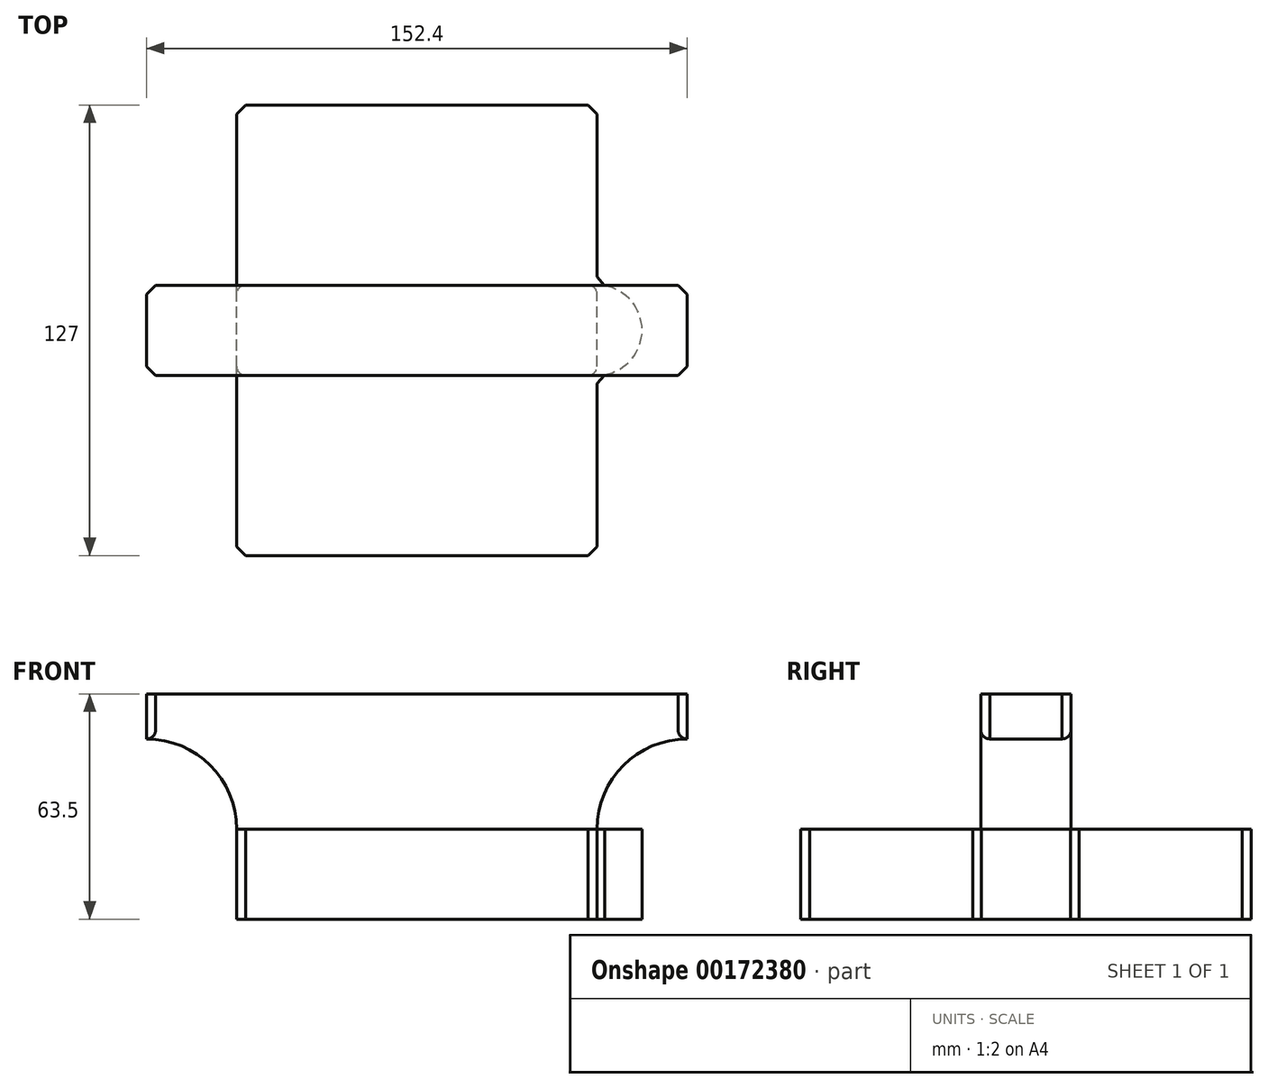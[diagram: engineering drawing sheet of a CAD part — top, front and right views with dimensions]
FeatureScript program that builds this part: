
annotation { "Feature Type Name" : "Feature", "Feature Type Description" : "" }
export const myFeature = defineFeature(function(context is Context, id is Id, definition is map)
    precondition{}
    {
        {
            var Q0;
            Q0=qCreatedBy(makeId("Front.planeOp"),FACE);
            var sketch = newSketch(context, id + "F0", { "sketchPlane" : qUnion([Q0])});
            skLineSegment(sketch, "E0.bottom", {"start": v(50.8, 12.7) * mm, "end": v(-50.8, 12.7) * mm});
            skLineSegment(sketch, "E0.top", {"start": v(50.8, -12.7) * mm, "end": v(-50.8, -12.7) * mm});
            skLineSegment(sketch, "E0.left", {"start": v(50.8, 12.7) * mm, "end": v(50.8, -12.7) * mm});
            skLineSegment(sketch, "E0.right", {"start": v(-50.8, 12.7) * mm, "end": v(-50.8, -12.7) * mm});
            skPoint(sketch, "E0.middle", {"position": v(0, 0) * mm});
            skLineSegment(sketch, "E1.bottom", {"start": v(76.2, 38.1) * mm, "end": v(-76.2, 38.1) * mm});
            skLineSegment(sketch, "E1.top", {"start": v(76.2, 50.8) * mm, "end": v(-76.2, 50.8) * mm});
            skLineSegment(sketch, "E1.left", {"start": v(76.2, 38.1) * mm, "end": v(76.2, 50.8) * mm});
            skLineSegment(sketch, "E1.right", {"start": v(-76.2, 38.1) * mm, "end": v(-76.2, 50.8) * mm});
            skPoint(sketch, "E1.middle", {"position": v(0, 44.45) * mm});
            skArc(sketch, "E2", {"start": v(-50.8, 12.7) * mm, "mid": v(-58.24, 30.66) * mm, "end": v(-76.2, 38.1) * mm});
            skArc(sketch, "E3", {"start": v(50.8, 12.7) * mm, "mid": v(58.24, 30.66) * mm, "end": v(76.2, 38.1) * mm});
            skLineSegment(sketch, "E4.bottom", {"start": v(50.8, 12.7) * mm, "end": v(63.5, 12.7) * mm});
            skLineSegment(sketch, "E4.top", {"start": v(50.8, -12.7) * mm, "end": v(63.5, -12.7) * mm});
            skLineSegment(sketch, "E4.right", {"start": v(63.5, 12.7) * mm, "end": v(63.5, -12.7) * mm});
            skSolve(sketch);
        }
        {
            var Q0;
            Q0=makeQuery(id+"F0.imprint","IMPRINT",FACE,{"disambiguationData":[TD([[makeQuery(id+"F0.imprint","IMPRINT",EDGE,{"derivedFrom":sQuery(id+"F0.wireOp",EDGE,"E0.bottom")}),1.0]])]});
            extrude(context, id + "F1", {"entities" : qUnion([Q0]), "endBound" : BoundingType.SYMMETRIC, "depth" : 127 * mm});
        }
        {
            var Q0;
            Q0=makeQuery(id+"F0.imprint","IMPRINT",FACE,{"disambiguationData":[TD([[makeQuery(id+"F0.imprint","IMPRINT",EDGE,{"derivedFrom":sQuery(id+"F0.wireOp",EDGE,"E0.bottom")}),-1.0]])]});
            var Q1;
            Q1=makeQuery(id+"F0.imprint","IMPRINT",FACE,{"disambiguationData":[TD([[makeQuery(id+"F0.imprint","IMPRINT",EDGE,{"derivedFrom":sQuery(id+"F0.wireOp",EDGE,"E1.bottom")}),-1.0]])]});
            extrude(context, id + "F2", {"entities" : qUnion([Q0, Q1]), "operationType" : NewBodyOperationType.ADD, "endBound" : BoundingType.SYMMETRIC, "depth" : 25.4 * mm});
        }
        {
            var Q0;
            Q0=makeQuery(id+"F0.imprint","IMPRINT",FACE,{"disambiguationData":[TD([[makeQuery(id+"F0.imprint","IMPRINT",EDGE,{"derivedFrom":sQuery(id+"F0.wireOp",EDGE,"E4.bottom")}),-1.0]])]});
            var Q1;
            Q1=sQuery(id+"F0.wireOp",EDGE,"E0.left");
            revolve(context, id + "F3", {"operationType" : NewBodyOperationType.ADD, "entities" : qUnion([Q0]), "axis" : qUnion([Q1]), "revolveType" : RevolveType.FULL});
        }
        {
            var Q0;
            Q0=makeQuery(id+"F1.opExtrude","CAP_EDGE",EDGE,{"disambiguationData":[OSD([sQuery(id+"F0.wireOp",EDGE,"E0.left")])],"isStart":false});
            var Q1;
            Q1=makeQuery(id+"F1.opExtrude","CAP_EDGE",EDGE,{"disambiguationData":[OSD([sQuery(id+"F0.wireOp",EDGE,"E0.right")])],"isStart":false});
            var Q2;
            Q2=makeQuery(id+"F3.boolean.opBoolean","INTERSECT",EDGE,{"disambiguationData":[OD(1.0)],"derivedFrom":[makeQuery(id+"F1.opExtrude","SWEPT_FACE",FACE,{"disambiguationData":[OSD([sQuery(id+"F0.wireOp",EDGE,"E0.left")])]}),makeQuery(id+"F3.opRevolve","SWEPT_FACE",FACE,{"disambiguationData":[OSD([sQuery(id+"F0.wireOp",EDGE,"E4.right")])]})]});
            var Q3;
            Q3=makeQuery(id+"F2.opExtrude","CAP_EDGE",EDGE,{"disambiguationData":[OSD([sQuery(id+"F0.wireOp",EDGE,"E1.left")])],"isStart":false});
            var Q4;
            Q4=makeQuery(id+"F2.opExtrude","CAP_EDGE",EDGE,{"disambiguationData":[OSD([sQuery(id+"F0.wireOp",EDGE,"E1.left")])],"isStart":true});
            var Q5;
            Q5=makeQuery(id+"F3.boolean.opBoolean","INTERSECT",EDGE,{"disambiguationData":[OD(0.0)],"derivedFrom":[makeQuery(id+"F1.opExtrude","SWEPT_FACE",FACE,{"disambiguationData":[OSD([sQuery(id+"F0.wireOp",EDGE,"E0.left")])]}),makeQuery(id+"F3.opRevolve","SWEPT_FACE",FACE,{"disambiguationData":[OSD([sQuery(id+"F0.wireOp",EDGE,"E4.right")])]})]});
            var Q6;
            Q6=makeQuery(id+"F1.opExtrude","CAP_EDGE",EDGE,{"disambiguationData":[OSD([sQuery(id+"F0.wireOp",EDGE,"E0.left")])],"isStart":true});
            var Q7;
            Q7=makeQuery(id+"F1.opExtrude","CAP_EDGE",EDGE,{"disambiguationData":[OSD([sQuery(id+"F0.wireOp",EDGE,"E0.right")])],"isStart":true});
            var Q8;
            Q8=makeQuery(id+"F2.opExtrude","CAP_EDGE",EDGE,{"disambiguationData":[OSD([sQuery(id+"F0.wireOp",EDGE,"E1.right")])],"isStart":true});
            var Q9;
            Q9=makeQuery(id+"F2.opExtrude","CAP_EDGE",EDGE,{"disambiguationData":[OSD([sQuery(id+"F0.wireOp",EDGE,"E1.right")])],"isStart":false});
            chamfer(context, id + "F4", {"entities" : qUnion([Q0, Q1, Q2, Q3, Q4, Q5, Q6, Q7, Q8, Q9]), "width" : 2.54 * mm, "tangentPropagation" : true});
        }
        {
            var Q0;
            Q0=makeQuery(id+"F2.opExtrude","CAP_EDGE",EDGE,{"disambiguationData":[OSD([sQuery(id+"F0.wireOp",EDGE,"E3")])],"isStart":false});
            var Q1;
            Q1=makeQuery(id+"F2.opExtrude","CAP_EDGE",EDGE,{"disambiguationData":[OSD([sQuery(id+"F0.wireOp",EDGE,"E3")])],"isStart":true});
            var Q2;
            Q2=makeQuery(id+"F2.opExtrude","CAP_EDGE",EDGE,{"disambiguationData":[OSD([sQuery(id+"F0.wireOp",EDGE,"E2")])],"isStart":false});
            var Q3;
            Q3=makeQuery(id+"F2.opExtrude","CAP_EDGE",EDGE,{"disambiguationData":[OSD([sQuery(id+"F0.wireOp",EDGE,"E2")])],"isStart":true});
            fillet(context, id + "F5", {"entities" : qUnion([Q0, Q1, Q2, Q3]), "radius" : 2.54 * mm, "tangentPropagation" : true, "allowEdgeOverflow" : false});
        }
    });
